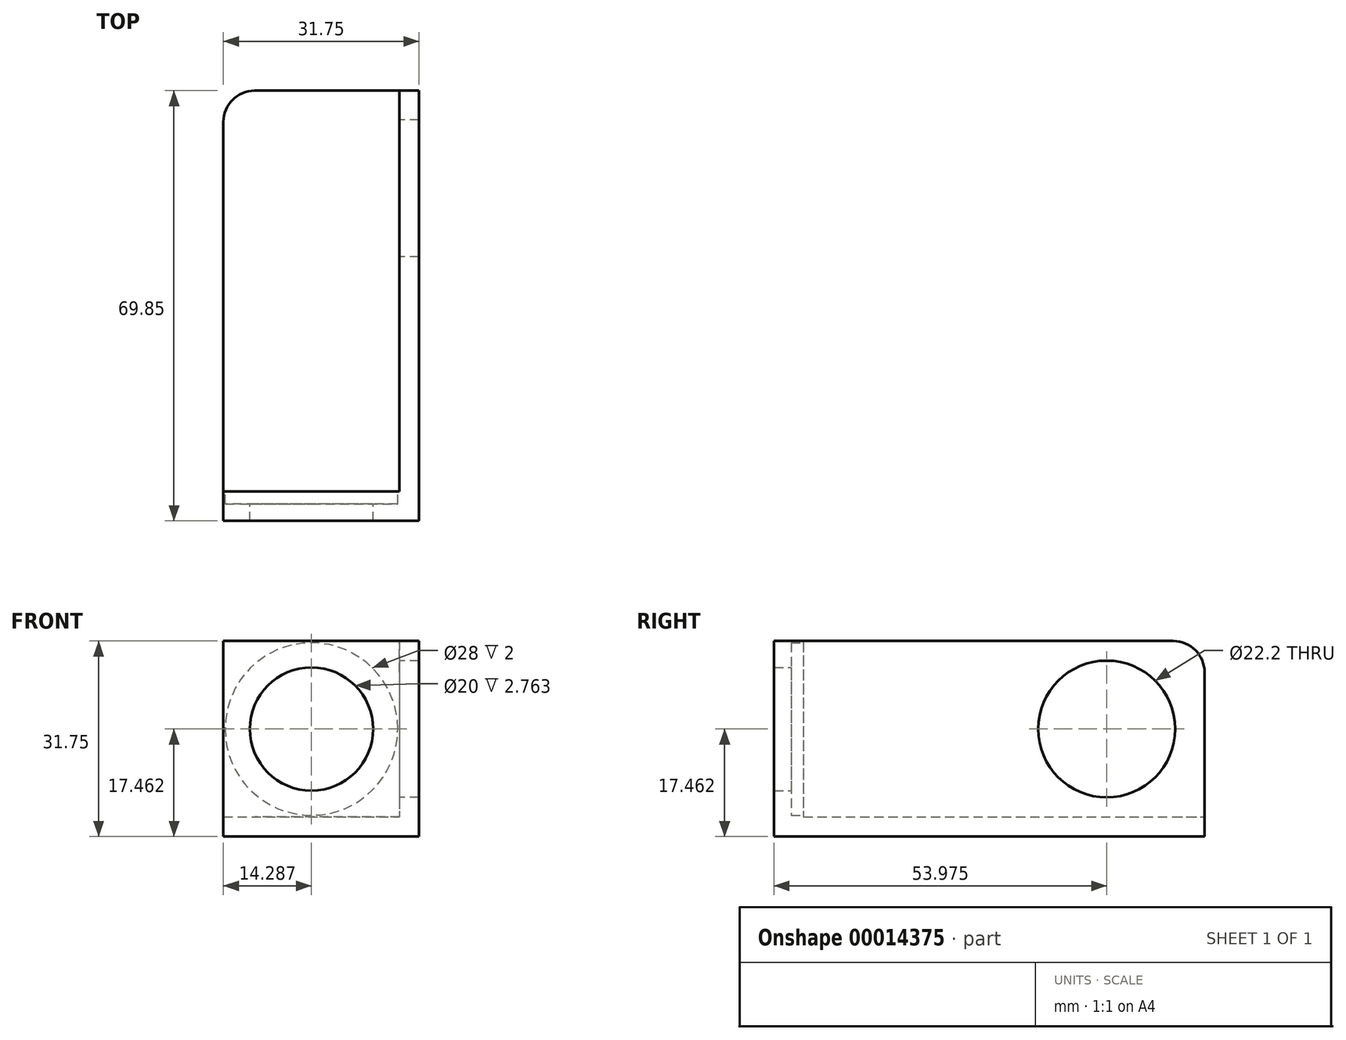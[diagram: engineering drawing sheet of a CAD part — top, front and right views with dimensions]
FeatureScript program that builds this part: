
annotation { "Feature Type Name" : "Feature", "Feature Type Description" : "" }
export const myFeature = defineFeature(function(context is Context, id is Id, definition is map)
    precondition{}
    {
        {
            var Q0;
            Q0=qCreatedBy(makeId("Front.planeOp"),FACE);
            var sketch = newSketch(context, id + "F0", { "sketchPlane" : qUnion([Q0])});
            skLineSegment(sketch, "E0", {"start": v(0, 0) * mm, "end": v(31.75, 0) * mm});
            skLineSegment(sketch, "E1", {"start": v(31.75, 0) * mm, "end": v(31.75, 31.75) * mm});
            skLineSegment(sketch, "E2", {"start": v(31.75, 31.75) * mm, "end": v(28.57, 31.75) * mm});
            skLineSegment(sketch, "E3", {"start": v(28.57, 31.75) * mm, "end": v(28.58, 3.18) * mm});
            skLineSegment(sketch, "E4", {"start": v(28.58, 3.18) * mm, "end": v(0, 3.18) * mm});
            skLineSegment(sketch, "E5", {"start": v(0, 3.18) * mm, "end": v(0, 0) * mm});
            skSolve(sketch);
        }
        {
            var Q0;
            Q0=qSketchRegion(id+"F0",true);
            extrude(context, id + "F1", {"entities" : qUnion([Q0]), "depth" : 69.85 * mm});
        }
        {
            var Q0;
            Q0=makeQuery(id+"F1.opExtrude","SWEPT_FACE",FACE,{"disambiguationData":[OSD([sQuery(id+"F0.wireOp",EDGE,"E4")])]});
            var sketch = newSketch(context, id + "F2", { "sketchPlane" : qUnion([Q0])});
            skLineSegment(sketch, "E6.bottom", {"start": v(0, -69.85) * mm, "end": v(28.58, -69.85) * mm});
            skLineSegment(sketch, "E6.top", {"start": v(0, -65.09) * mm, "end": v(28.58, -65.09) * mm});
            skLineSegment(sketch, "E6.left", {"start": v(0, -69.85) * mm, "end": v(0, -65.09) * mm});
            skLineSegment(sketch, "E6.right", {"start": v(28.58, -69.85) * mm, "end": v(28.58, -65.09) * mm});
            skSolve(sketch);
        }
        {
            var Q0;
            Q0=qSketchRegion(id+"F2",true);
            var Q1;
            Q1=makeQuery(id+"F1.opExtrude","SWEPT_FACE",FACE,{"disambiguationData":[OSD([sQuery(id+"F0.wireOp",EDGE,"E2")])]});
            extrude(context, id + "F3", {"entities" : qUnion([Q0]), "operationType" : NewBodyOperationType.ADD, "endBound" : BoundingType.UP_TO_SURFACE, "endBoundEntityFace" : qUnion([Q1]), "depth" : 25 * mm});
        }
        {
            var Q0;
            Q0=makeQuery(id+"F3.opExtrude","SWEPT_FACE",FACE,{"disambiguationData":[OSD([sQuery(id+"F2.wireOp",EDGE,"E6.top")])]});
            var sketch = newSketch(context, id + "F4", { "sketchPlane" : qUnion([Q0])});
            skLineSegment(sketch, "E7", {"start": v(-28.58, 17.46) * mm, "end": v(0, 17.46) * mm, "construction": true});
            skCircle(sketch, "E8", {"center": v(-14.29, 17.46) * mm, "radius": 14 * mm});
            skSolve(sketch);
        }
        {
            var Q0;
            Q0=qSketchRegion(id+"F4",true);
            extrude(context, id + "F5", {"entities" : qUnion([Q0]), "operationType" : NewBodyOperationType.REMOVE, "oppositeDirection" : true, "depth" : 2 * mm});
        }
        {
            var Q0;
            Q0=makeQuery(id+"F5.boolean.opBoolean","COPY",FACE,{"derivedFrom":makeQuery(id+"F5.opExtrude","CAP_FACE",FACE,{"disambiguationData":[OSD([sQuery(id+"F4.wireOp",EDGE,"E8")])],"isStart":false})});
            var sketch = newSketch(context, id + "F6", { "sketchPlane" : qUnion([Q0])});
            skCircle(sketch, "E9", {"center": v(-14.29, 17.46) * mm, "radius": 10 * mm});
            skSolve(sketch);
        }
        {
            var Q0;
            Q0=qSketchRegion(id+"F6",true);
            extrude(context, id + "F7", {"entities" : qUnion([Q0]), "operationType" : NewBodyOperationType.REMOVE, "endBound" : BoundingType.UP_TO_NEXT, "oppositeDirection" : true, "depth" : 25 * mm});
        }
        {
            var Q0;
            Q0=makeQuery(id+"F1.opExtrude","SWEPT_FACE",FACE,{"disambiguationData":[OSD([sQuery(id+"F0.wireOp",EDGE,"E3")])]});
            var sketch = newSketch(context, id + "F8", { "sketchPlane" : qUnion([Q0])});
            skPoint(sketch, "E10", {"position": v(15.88, 17.46) * mm});
            skCircle(sketch, "E11", {"center": v(15.88, 17.46) * mm, "radius": 11.1 * mm});
            skLineSegment(sketch, "E12", {"start": v(65.09, 17.46) * mm, "end": v(0, 17.46) * mm});
            skSolve(sketch);
        }
        {
            var Q0;
            Q0=qSketchRegion(id+"F8",true);
            extrude(context, id + "F9", {"entities" : qUnion([Q0]), "operationType" : NewBodyOperationType.REMOVE, "endBound" : BoundingType.UP_TO_NEXT, "oppositeDirection" : true, "depth" : 25 * mm});
        }
        {
            var Q0;
            Q0=makeQuery(id+"F1.opExtrude","CAP_EDGE",EDGE,{"disambiguationData":[OSD([sQuery(id+"F0.wireOp",EDGE,"E5")])],"isStart":true});
            var Q1;
            Q1=makeQuery(id+"F3.opExtrude","TWEAK_EDGE",EDGE,{"derivedFrom":[makeQuery(id+"F1.opExtrude","SWEPT_FACE",FACE,{"disambiguationData":[OSD([sQuery(id+"F0.wireOp",EDGE,"E2")])]}),makeQuery(id+"F2.imprint","IMPRINT",EDGE,{"derivedFrom":sQuery(id+"F2.wireOp",EDGE,"E6.left")})]});
            var Q2;
            Q2=makeQuery(id+"F1.opExtrude","CAP_EDGE",EDGE,{"disambiguationData":[OSD([sQuery(id+"F0.wireOp",EDGE,"E2")])],"isStart":true});
            fillet(context, id + "F10", {"entities" : qUnion([Q0, Q1, Q2]), "radius" : 5.08 * mm, "tangentPropagation" : true, "allowEdgeOverflow" : false});
        }
    });
